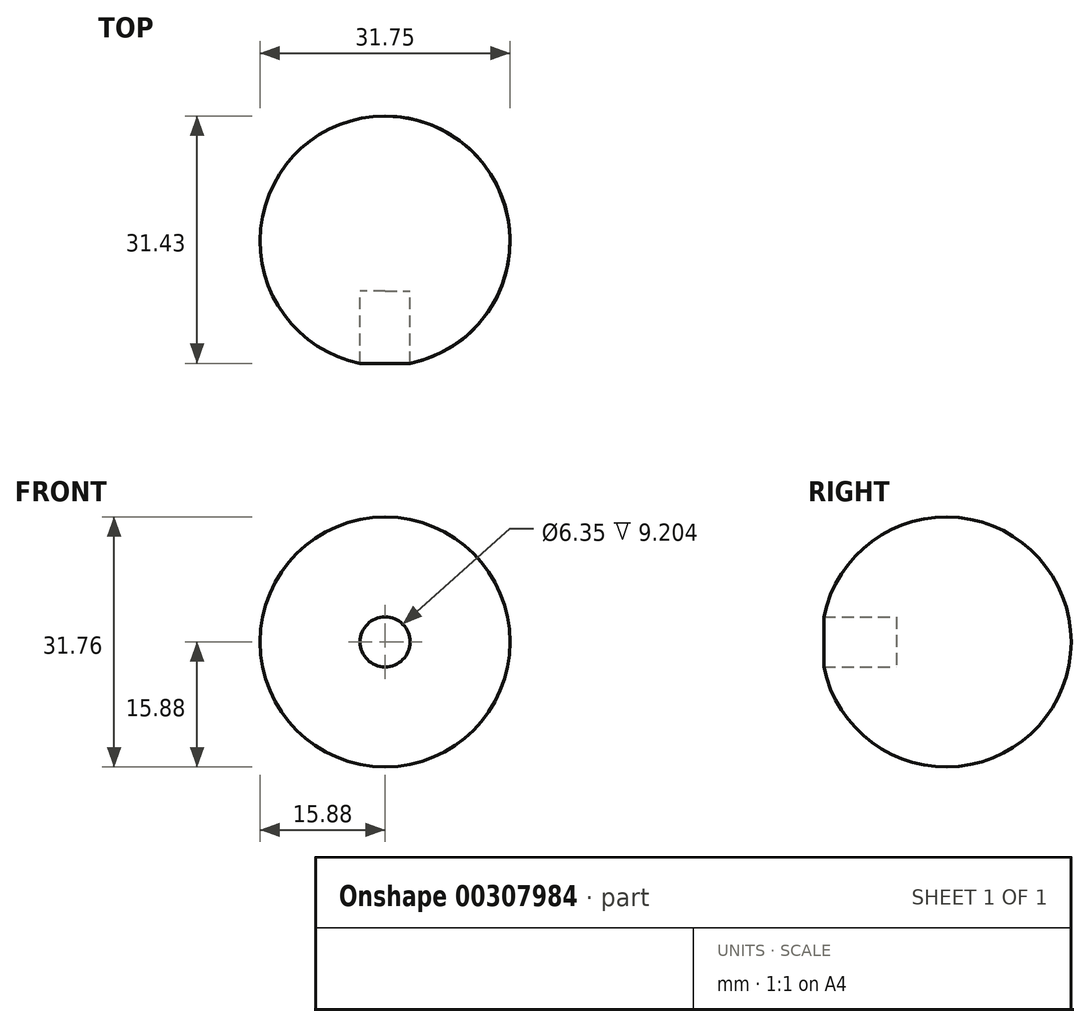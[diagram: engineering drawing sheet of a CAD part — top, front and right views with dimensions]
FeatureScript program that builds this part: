
annotation { "Feature Type Name" : "Feature", "Feature Type Description" : "" }
export const myFeature = defineFeature(function(context is Context, id is Id, definition is map)
    precondition{}
    {
        {
            var Q0;
            Q0=qCreatedBy(makeId("Front.planeOp"),FACE);
            var sketch = newSketch(context, id + "F0", { "sketchPlane" : qUnion([Q0])});
            skCircle(sketch, "E0", {"center": v(0, 0) * mm, "radius": 15.88 * mm});
            skSolve(sketch);
        }
        {
            var Q0;
            Q0=qCreatedBy(makeId("Top.planeOp"),FACE);
            var sketch = newSketch(context, id + "F1", { "sketchPlane" : qUnion([Q0])});
            skArc(sketch, "E1", {"start": v(0, 15.88) * mm, "mid": v(-15.88, 0) * mm, "end": v(0, -15.88) * mm});
            skLineSegment(sketch, "E2", {"start": v(0, 15.88) * mm, "end": v(0, -15.88) * mm});
            skSolve(sketch);
        }
        {
            var Q0;
            Q0=makeQuery(id+"F1.imprint","IMPRINT",FACE,{"disambiguationData":[TD([[makeQuery(id+"F1.imprint","IMPRINT",EDGE,{"derivedFrom":sQuery(id+"F1.wireOp",EDGE,"E1")}),1.0]])]});
            var Q1;
            Q1=sQuery(id+"F0.wireOp",EDGE,"E0");
            revolve(context, id + "F2", {"entities" : qUnion([Q0]), "axis" : qUnion([Q1]), "revolveType" : RevolveType.FULL});
        }
        {
            var Q0;
            Q0=qCreatedBy(makeId("Front.planeOp"),FACE);
            cPlane(context, id + "F3", {"entities" : qUnion([Q0]), "cplaneType" : CPlaneType.OFFSET, "offset" : 6.35 * mm, "width" : 152.4 * mm, "height" : 152.4 * mm});
        }
        {
            var Q0;
            Q0=qCreatedBy(id+"F3.planeOp",FACE);
            var sketch = newSketch(context, id + "F4", { "sketchPlane" : qUnion([Q0])});
            skCircle(sketch, "E3", {"center": v(0, 0) * mm, "radius": 3.18 * mm});
            skSolve(sketch);
        }
        {
            var Q0;
            Q0 = qSketchRegion(id + "F4", true);
            extrude(context, id + "F5", {"entities" : qUnion([Q0]), "depth" : 25.4 * mm});
        }
        {
            var Q0;
            Q0=makeQuery(id+"F5.opExtrude","SWEPT_BODY",BODY,{"disambiguationData":[OSD([sQuery(id+"F4.wireOp",EDGE,"E3")])]});
            var Q1;
            Q1=makeQuery(id+"F2.opRevolve","SWEPT_BODY",BODY,{"disambiguationData":[OSD([sQuery(id+"F1.wireOp",EDGE,"E1"),sQuery(id+"F1.wireOp",EDGE,"E2")])]});
            booleanBodies(context, id + "F6", {"operationType" : BooleanOperationType.SUBTRACTION, "tools" : qUnion([Q0]), "targets" : qUnion([Q1])});
        }
    });
